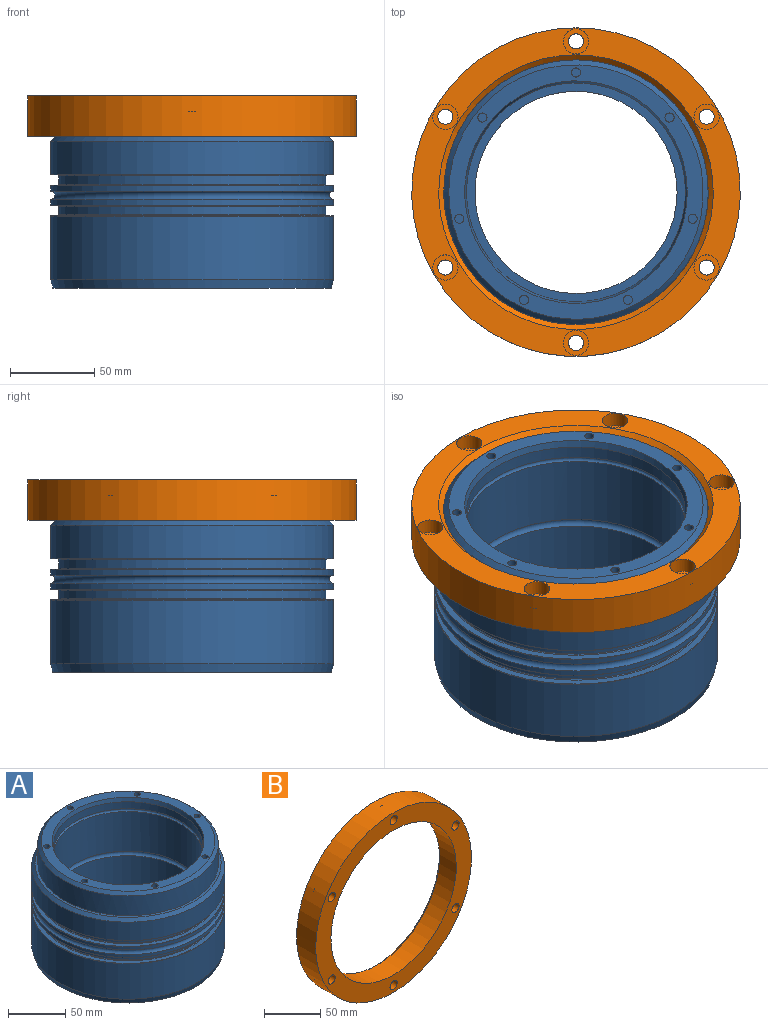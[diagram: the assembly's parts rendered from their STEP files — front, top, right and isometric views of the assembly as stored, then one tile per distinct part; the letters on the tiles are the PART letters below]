
ASSEMBLY  parts=2 mates=1
PART A: 50 faces, bbox 185.7x185.7x114 mm
  f0: torus R=65mm, axis (0,0,1), area 1943.7mm2, adj f23,f24,f48
  f1: torus R=79.8mm, axis (0,0,1), area 392.2mm2, adj f2,f31
  f2: cylinder r=79.3mm len=158.6mm, axis (0,0,1), area 2541.1mm2, adj f1,f3
  f3: torus R=79.8mm, axis (0,0,1), area 392.2mm2, adj f2,f4
  f4: plane 167.6x167.6mm, normal (0,0,1), area 2055.9mm2, adj f3,f5
  f5: torus R=83.8mm, axis (0,0,1), area 165.7mm2, adj f4,f6
  f6: cylinder r=84mm len=168mm, axis (0,0,1), area 1741.7mm2, adj f5,f7
  f7: torus R=84mm, axis (0,0,1), area 4066.7mm2, adj f6,f8
  f8: cylinder r=84mm len=168mm, axis (0,0,1), area 1741.7mm2, adj f7,f9
  f9: torus R=83.8mm, axis (0,0,1), area 165.7mm2, adj f8,f10
  f10: plane 167.6x167.6mm, normal (0,0,-1), area 2055.9mm2, adj f9,f11
  f11: torus R=79.8mm, axis (0,0,1), area 392.2mm2, adj f10,f12
  f12: cylinder r=79.3mm len=158.6mm, axis (0,0,1), area 2541.1mm2, adj f11,f13
  f13: torus R=79.8mm, axis (0,0,1), area 392.2mm2, adj f12,f14
  f14: plane 167.6x167.6mm, normal (0,0,1), area 2055.9mm2, adj f13,f15
  f15: torus R=83.8mm, axis (0,0,1), area 165.7mm2, adj f14,f16
  f16: cylinder r=84mm len=168mm, axis (0,0,1), area 19950.4mm2, adj f15,f17
  f17: cone r=84mm half-angle=15deg, axis (0,0,1), area 2656.5mm2, adj f16,f18
  f18: plane 165.37x165.37mm, normal (0,0,-1), area 10169.8mm2, adj f17,f19
  f19: cylinder r=60mm len=120mm, axis (0,0,1), area 5277.9mm2, adj f18,f20
  f20: plane 130x130mm, normal (0,0,1), area 1963.5mm2, adj f19,f21
  f21: cylinder r=65mm len=130mm, axis (0,0,1), area 15723.7mm2, adj f20,f22
  f22: torus R=65mm, axis (0,0,1), area 3286.2mm2, adj f21,f23
  f23: cylinder r=65mm len=130mm, axis (0,0,1), area 17153.1mm2, adj f0,f22
  f24: cylinder r=65mm len=130mm, axis (0,0,1), area 3063.1mm2, adj f0,f25
  f25: cone r=66.07mm half-angle=15deg, axis (0,0,1), area 1705.2mm2, adj f24,f26
  f26: plane 151x151mm, normal (0,0,1), area 4033mm2, adj f25,f32,f34,f36,f38,f40,f42,f44
  f27: cylinder r=78.5mm len=157mm, axis (0,0,1), area 10357.8mm2, adj f28,f46
  f28: plane 162x162mm, normal (0,0,1), area 1252.7mm2, adj f27,f47
  f29: cylinder r=84mm len=168mm, axis (0,0,1), area 10397.4mm2, adj f30,f47
  f30: torus R=83.8mm, axis (0,0,1), area 165.7mm2, adj f29,f31
  f31: plane 167.6x167.6mm, normal (0,0,-1), area 2055.9mm2, adj f1,f30
  f32: cylinder r=2.7mm len=25mm, axis (0,0,1), area 424.1mm2, adj f26,f33
  f33: plane 5.4x5.4mm, normal (0,0,1), area 22.9mm2, adj f32
  f34: cylinder r=2.7mm len=25mm, axis (0,0,1), area 424.1mm2, adj f26,f35
  f35: plane 5.4x5.4mm, normal (0,0,1), area 22.9mm2, adj f34
  f36: cylinder r=2.7mm len=25mm, axis (0,0,1), area 424.1mm2, adj f26,f37
  f37: plane 5.4x5.4mm, normal (0,0,1), area 22.9mm2, adj f36
  f38: cylinder r=2.7mm len=25mm, axis (0,0,1), area 424.1mm2, adj f26,f39
  f39: plane 5.4x5.4mm, normal (0,0,1), area 22.9mm2, adj f38
  f40: cylinder r=2.7mm len=25mm, axis (0,0,1), area 424.1mm2, adj f26,f41
  f41: plane 5.4x5.4mm, normal (0,0,1), area 22.9mm2, adj f40
  f42: cylinder r=2.7mm len=25mm, axis (0,0,1), area 424.1mm2, adj f26,f43
  f43: plane 5.4x5.4mm, normal (0,0,1), area 22.9mm2, adj f42
  f44: cylinder r=2.7mm len=25mm, axis (0,0,1), area 424.1mm2, adj f26,f45
  f45: plane 5.4x5.4mm, normal (0,0,1), area 22.9mm2, adj f44
  f46: cone r=75.5mm half-angle=45deg, axis (0,0,-1), area 2052.6mm2, adj f26,f27
  f47: cone r=81mm half-angle=45deg, axis (0,0,-1), area 2199.2mm2, adj f28,f29
  f48: cylinder r=1.5mm len=6.75mm, axis (0,1,0), area 54.7mm2, adj f0,f49
  f49: plane 3x3mm, normal (0,1,0), area 7.1mm2, adj f48
PART B: 23 faces, bbox 195x24x195 mm
  f0: cylinder r=4.5mm len=15mm, axis (0,1,0), area 424.1mm2, adj f8,f14
  f1: cylinder r=4.5mm len=15mm, axis (0,1,0), area 424.1mm2, adj f8,f22
  f2: cylinder r=4.5mm len=15mm, axis (0,1,0), area 424.1mm2, adj f8,f12
  f3: cylinder r=4.5mm len=15mm, axis (0,1,0), area 424.1mm2, adj f8,f20
  f4: cylinder r=4.5mm len=15mm, axis (0,1,0), area 424.1mm2, adj f8,f18
  f5: cylinder r=97.5mm len=195mm, axis (0,1,0), area 14702.7mm2, adj f8,f9
  f6: cylinder r=78.5mm len=157mm, axis (0,1,0), area 10357.8mm2, adj f8,f10
  f7: cylinder r=4.5mm len=15mm, axis (0,1,0), area 424.1mm2, adj f8,f16
  f8: plane 195x195mm, normal (0,-1,0), area 10123.8mm2, adj f0,f1,f2,f3,f4,f5,f6,f7
  f9: plane 195x195mm, normal (0,1,0), area 7937.2mm2, adj f5,f10,f11,f13,f15,f17,f19,f21
  f10: cone r=81.5mm half-angle=45deg, axis (0,1,0), area 2132.6mm2, adj f6,f9
  f11: cylinder r=7.5mm len=15mm, axis (0,1,0), area 424.1mm2, adj f9,f12
  f12: plane 15x15mm, normal (0,1,0), area 113.1mm2, adj f2,f11
  f13: cylinder r=7.5mm len=15mm, axis (0,1,0), area 424.1mm2, adj f9,f14
  f14: plane 15x15mm, normal (0,1,0), area 113.1mm2, adj f0,f13
  f15: cylinder r=7.5mm len=15mm, axis (0,1,0), area 424.1mm2, adj f9,f16
  f16: plane 15x15mm, normal (0,1,0), area 113.1mm2, adj f7,f15
  f17: cylinder r=7.5mm len=15mm, axis (0,1,0), area 424.1mm2, adj f9,f18
  f18: plane 15x15mm, normal (0,1,0), area 113.1mm2, adj f4,f17
  f19: cylinder r=7.5mm len=15mm, axis (0,1,0), area 424.1mm2, adj f9,f20
  f20: plane 15x15mm, normal (0,1,0), area 113.1mm2, adj f3,f19
  f21: cylinder r=7.5mm len=15mm, axis (0,1,0), area 424.1mm2, adj f9,f22
  f22: plane 15x15mm, normal (0,1,0), area 113.1mm2, adj f1,f21
PLACE A t=(-192.51,185.64,-41.17)mm
PLACE B rot(axis=(1,0,0),90deg) t=(-375.76,236.99,408.58)mm
MATE fastened B.f5 <-> A.f2  axis (0,0,-1) through (37.94,185.64,384.58)mm
